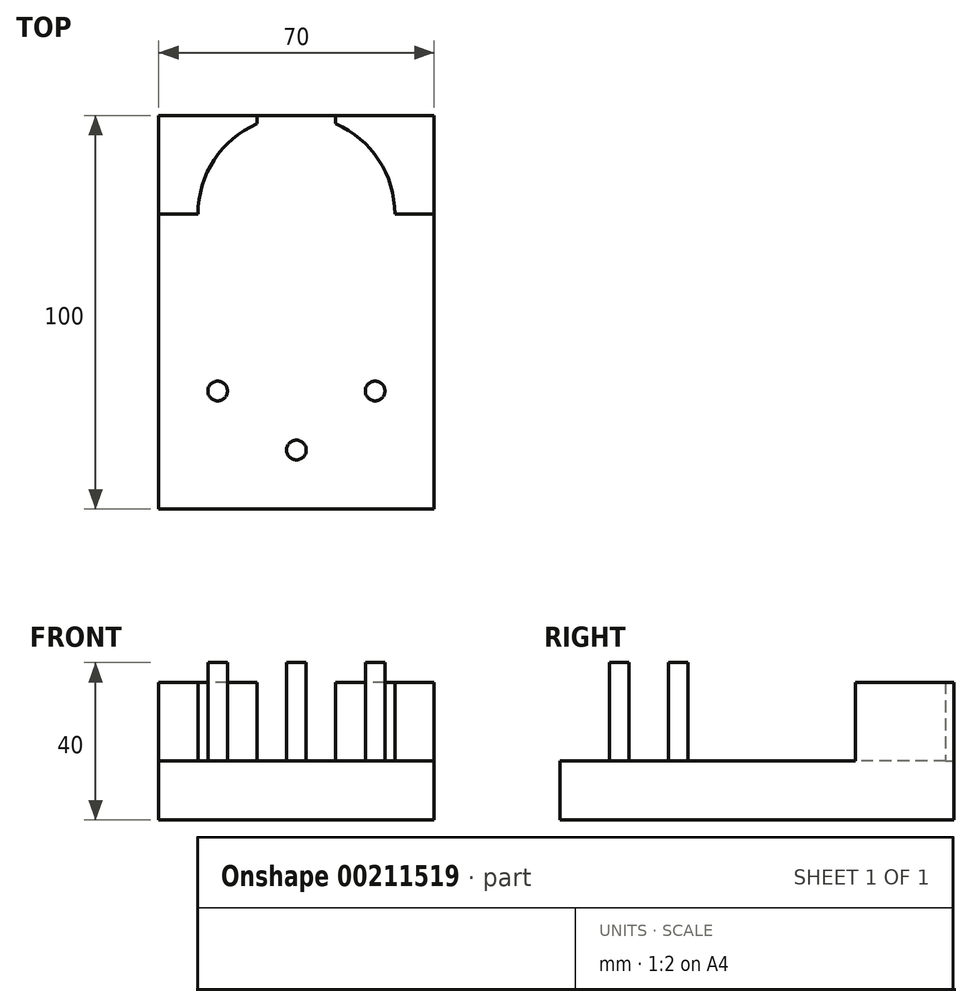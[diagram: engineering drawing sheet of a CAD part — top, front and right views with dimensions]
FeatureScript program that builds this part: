
annotation { "Feature Type Name" : "Feature", "Feature Type Description" : "" }
export const myFeature = defineFeature(function(context is Context, id is Id, definition is map)
    precondition{}
    {
        {
            var Q0;
            Q0=qCreatedBy(makeId("Top.planeOp"),FACE);
            var sketch = newSketch(context, id + "F0", { "sketchPlane" : qUnion([Q0])});
            skLineSegment(sketch, "E0.bottom", {"start": v(-35, 50) * mm, "end": v(35, 50) * mm});
            skLineSegment(sketch, "E0.top", {"start": v(-35, -50) * mm, "end": v(35, -50) * mm});
            skLineSegment(sketch, "E0.left", {"start": v(-35, 50) * mm, "end": v(-35, -50) * mm});
            skLineSegment(sketch, "E0.right", {"start": v(35, 50) * mm, "end": v(35, -50) * mm});
            skPoint(sketch, "E0.middle", {"position": v(0, 0) * mm});
            skSolve(sketch);
        }
        {
            var Q0;
            Q0=makeQuery(id+"F0.imprint","IMPRINT",FACE,{"disambiguationData":[TD([[makeQuery(id+"F0.imprint","IMPRINT",EDGE,{"derivedFrom":sQuery(id+"F0.wireOp",EDGE,"E0.bottom")}),-1.0]])]});
            extrude(context, id + "F1", {"entities" : qUnion([Q0]), "oppositeDirection" : true, "depth" : 15 * mm});
        }
        {
            var Q0;
            Q0=makeQuery(id+"F1.opExtrude","CAP_FACE",FACE,{"disambiguationData":[OSD([sQuery(id+"F0.wireOp",EDGE,"E0.bottom"),sQuery(id+"F0.wireOp",EDGE,"E0.top"),sQuery(id+"F0.wireOp",EDGE,"E0.left"),sQuery(id+"F0.wireOp",EDGE,"E0.right")])],"isStart":true});
            var sketch = newSketch(context, id + "F2", { "sketchPlane" : qUnion([Q0])});
            skArc(sketch, "E1", {"start": v(25, 25) * mm, "mid": v(20.92, 38.7) * mm, "end": v(10, 47.91) * mm});
            skLineSegment(sketch, "E2", {"start": v(-25, 25) * mm, "end": v(-35, 25) * mm});
            skLineSegment(sketch, "E3", {"start": v(-35, 25) * mm, "end": v(-35, 50) * mm});
            skLineSegment(sketch, "E4", {"start": v(-35, 50) * mm, "end": v(-10, 50) * mm});
            skLineSegment(sketch, "E5", {"start": v(10, 50) * mm, "end": v(35, 50) * mm});
            skLineSegment(sketch, "E6", {"start": v(35, 50) * mm, "end": v(35, 25) * mm});
            skLineSegment(sketch, "E7", {"start": v(35, 25) * mm, "end": v(25, 25) * mm});
            skLineSegment(sketch, "E8", {"start": v(-10, 47.91) * mm, "end": v(-10, 50) * mm});
            skPoint(sketch, "E9.start.orphan", {"position": v(0, 45.32) * mm});
            skArc(sketch, "E10.trimOffspring", {"start": v(-10, 47.91) * mm, "mid": v(-20.92, 38.7) * mm, "end": v(-25, 25) * mm});
            skLineSegment(sketch, "E11", {"start": v(10, 47.91) * mm, "end": v(10, 50) * mm});
            skPoint(sketch, "E12.orphan", {"position": v(0, 50) * mm});
            skSolve(sketch);
        }
        {
            var Q0;
            Q0=makeQuery(id+"F2.imprint","IMPRINT",FACE,{"disambiguationData":[TD([[makeQuery(id+"F2.imprint","IMPRINT",EDGE,{"derivedFrom":sQuery(id+"F2.wireOp",EDGE,"E2")}),-1.0]])]});
            var Q1;
            Q1=makeQuery(id+"F2.imprint","IMPRINT",FACE,{"disambiguationData":[TD([[makeQuery(id+"F2.imprint","IMPRINT",EDGE,{"derivedFrom":sQuery(id+"F2.wireOp",EDGE,"E1")}),-1.0]])]});
            extrude(context, id + "F3", {"entities" : qUnion([Q0, Q1]), "operationType" : NewBodyOperationType.ADD, "depth" : 20 * mm});
        }
        {
            var Q0;
            Q0=makeQuery(id+"F1.opExtrude","CAP_FACE",FACE,{"disambiguationData":[OSD([sQuery(id+"F0.wireOp",EDGE,"E0.bottom"),sQuery(id+"F0.wireOp",EDGE,"E0.top"),sQuery(id+"F0.wireOp",EDGE,"E0.left"),sQuery(id+"F0.wireOp",EDGE,"E0.right")])],"isStart":true});
            var sketch = newSketch(context, id + "F4", { "sketchPlane" : qUnion([Q0])});
            skCircle(sketch, "E13", {"center": v(0, -35) * mm, "radius": 2.5 * mm});
            skCircle(sketch, "E14", {"center": v(-20, -20) * mm, "radius": 2.5 * mm});
            skCircle(sketch, "E15", {"center": v(20, -20) * mm, "radius": 2.5 * mm});
            skSolve(sketch);
        }
        {
            var Q0;
            Q0=makeQuery(id+"F4.imprint","IMPRINT",FACE,{"disambiguationData":[TD([[makeQuery(id+"F4.imprint","IMPRINT",EDGE,{"derivedFrom":sQuery(id+"F4.wireOp",EDGE,"E14")}),1.0]])]});
            var Q1;
            Q1=makeQuery(id+"F4.imprint","IMPRINT",FACE,{"disambiguationData":[TD([[makeQuery(id+"F4.imprint","IMPRINT",EDGE,{"derivedFrom":sQuery(id+"F4.wireOp",EDGE,"E13")}),1.0]])]});
            var Q2;
            Q2=makeQuery(id+"F4.imprint","IMPRINT",FACE,{"disambiguationData":[TD([[makeQuery(id+"F4.imprint","IMPRINT",EDGE,{"derivedFrom":sQuery(id+"F4.wireOp",EDGE,"E15")}),1.0]])]});
            extrude(context, id + "F5", {"entities" : qUnion([Q0, Q1, Q2]), "operationType" : NewBodyOperationType.ADD, "depth" : 25 * mm});
        }
    });
